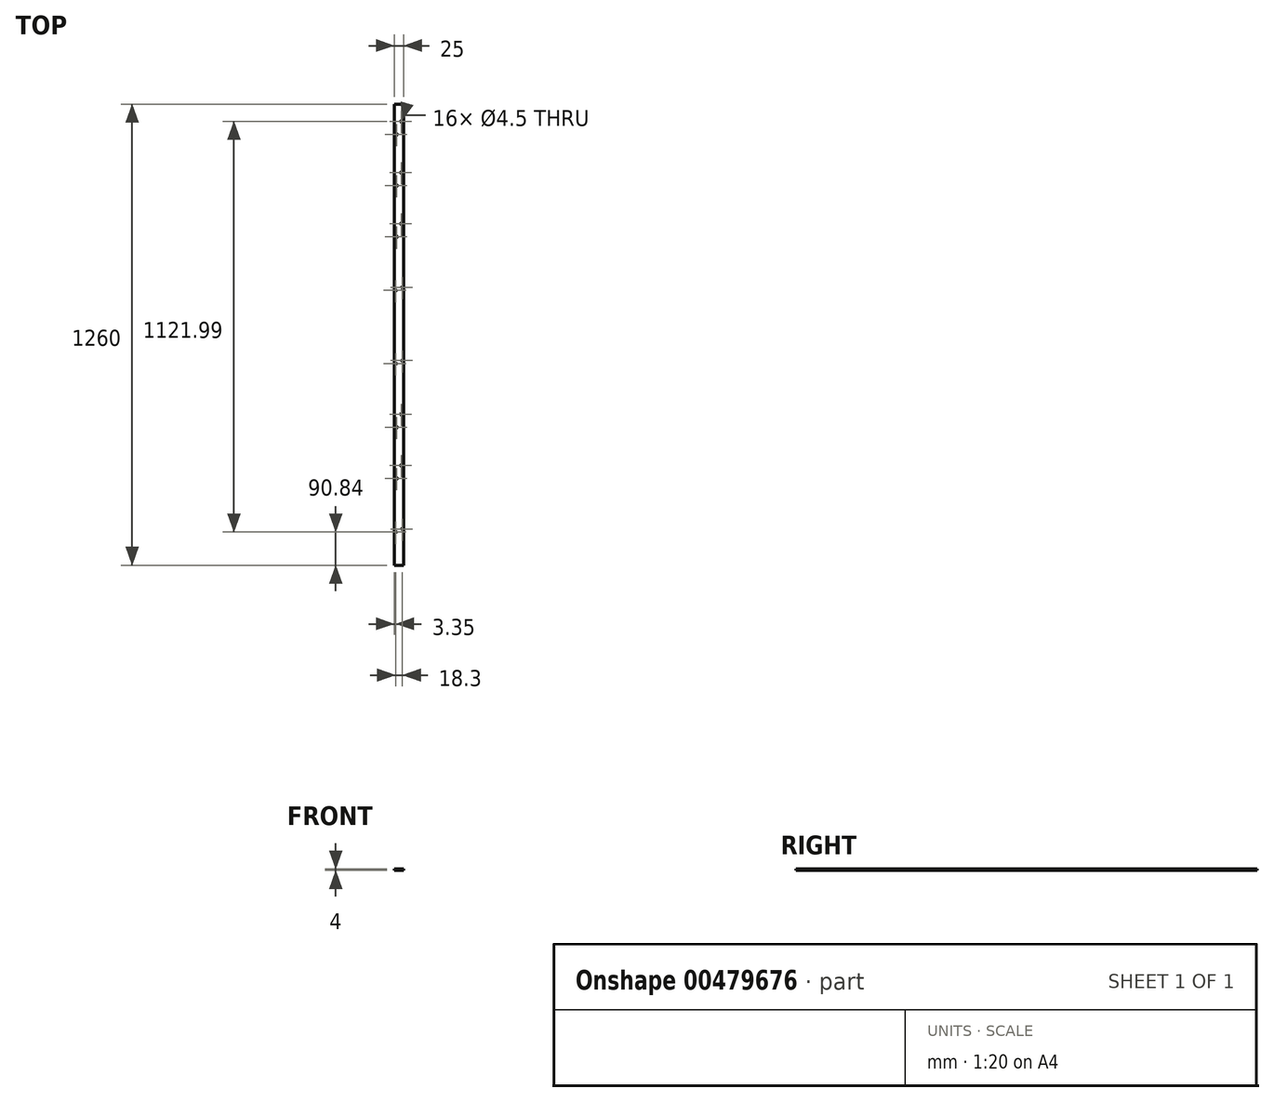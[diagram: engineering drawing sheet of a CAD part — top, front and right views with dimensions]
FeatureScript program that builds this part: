
annotation { "Feature Type Name" : "Feature", "Feature Type Description" : "" }
export const myFeature = defineFeature(function(context is Context, id is Id, definition is map)
    precondition{}
    {
        {
            var Q0;
            Q0=qCreatedBy(makeId("Top.planeOp"),FACE);
            var sketch = newSketch(context, id + "F0", { "sketchPlane" : qUnion([Q0])});
            skLineSegment(sketch, "E0.bottom", {"start": v(12.5, -630) * mm, "end": v(-12.5, -630) * mm});
            skLineSegment(sketch, "E0.top", {"start": v(12.5, 630) * mm, "end": v(-12.5, 630) * mm});
            skLineSegment(sketch, "E0.left", {"start": v(12.5, -630) * mm, "end": v(12.5, 630) * mm});
            skLineSegment(sketch, "E0.right", {"start": v(-12.5, -630) * mm, "end": v(-12.5, 630) * mm});
            skPoint(sketch, "E0.middle", {"position": v(0, 0) * mm});
            skCircle(sketch, "E1", {"center": v(6.25, 582.83) * mm, "radius": 2.25 * mm});
            skCircle(sketch, "E2", {"center": v(-6.25, 547.18) * mm, "radius": 2.25 * mm});
            skCircle(sketch, "E3.0.1.0", {"center": v(6.25, 442.83) * mm, "radius": 2.25 * mm});
            skCircle(sketch, "E3.0.1.1", {"center": v(-6.25, 407.18) * mm, "radius": 2.25 * mm});
            skCircle(sketch, "E3.0.2.0", {"center": v(6.25, 302.83) * mm, "radius": 2.25 * mm});
            skCircle(sketch, "E3.0.2.1", {"center": v(-6.25, 267.18) * mm, "radius": 2.25 * mm});
            skLineSegment(sketch, "E3.direction1", {"start": v(-6.25, 547.18) * mm, "end": v(18.75, 547.18) * mm, "construction": true});
            skLineSegment(sketch, "E3.direction2", {"start": v(-6.25, 547.18) * mm, "end": v(-6.25, 407.18) * mm, "construction": true});
            skCircle(sketch, "E4", {"center": v(9.15, 129.15) * mm, "radius": 2.25 * mm});
            skCircle(sketch, "E5", {"center": v(-9.15, 120.84) * mm, "radius": 2.25 * mm});
            skCircle(sketch, "E6.0.1.0", {"center": v(-9.15, -79.16) * mm, "radius": 2.25 * mm});
            skCircle(sketch, "E6.0.1.1", {"center": v(9.15, -70.85) * mm, "radius": 2.25 * mm});
            skLineSegment(sketch, "E6.direction1", {"start": v(-9.15, 120.84) * mm, "end": v(15.85, 120.84) * mm, "construction": true});
            skLineSegment(sketch, "E6.direction2", {"start": v(-9.15, 120.84) * mm, "end": v(-9.15, -79.16) * mm, "construction": true});
            skCircle(sketch, "E7", {"center": v(6.25, -217.17) * mm, "radius": 2.25 * mm});
            skCircle(sketch, "E8", {"center": v(-6.25, -252.82) * mm, "radius": 2.25 * mm});
            skCircle(sketch, "E9.0.1.0", {"center": v(6.25, -357.17) * mm, "radius": 2.25 * mm});
            skCircle(sketch, "E9.0.1.1", {"center": v(-6.25, -392.82) * mm, "radius": 2.25 * mm});
            skLineSegment(sketch, "E9.direction1", {"start": v(-6.25, -252.82) * mm, "end": v(18.75, -252.82) * mm, "construction": true});
            skLineSegment(sketch, "E9.direction2", {"start": v(-6.25, -252.82) * mm, "end": v(-6.25, -392.82) * mm, "construction": true});
            skCircle(sketch, "E10", {"center": v(9.15, -530.85) * mm, "radius": 2.25 * mm});
            skCircle(sketch, "E11", {"center": v(-9.15, -539.16) * mm, "radius": 2.25 * mm});
            skSolve(sketch);
        }
        {
            var Q0;
            Q0 = qSketchRegion(id + "F0", true);
            extrude(context, id + "F1", {"entities" : qUnion([Q0]), "depth" : 4 * mm, "offsetDistance" : 25 * mm});
        }
    });
